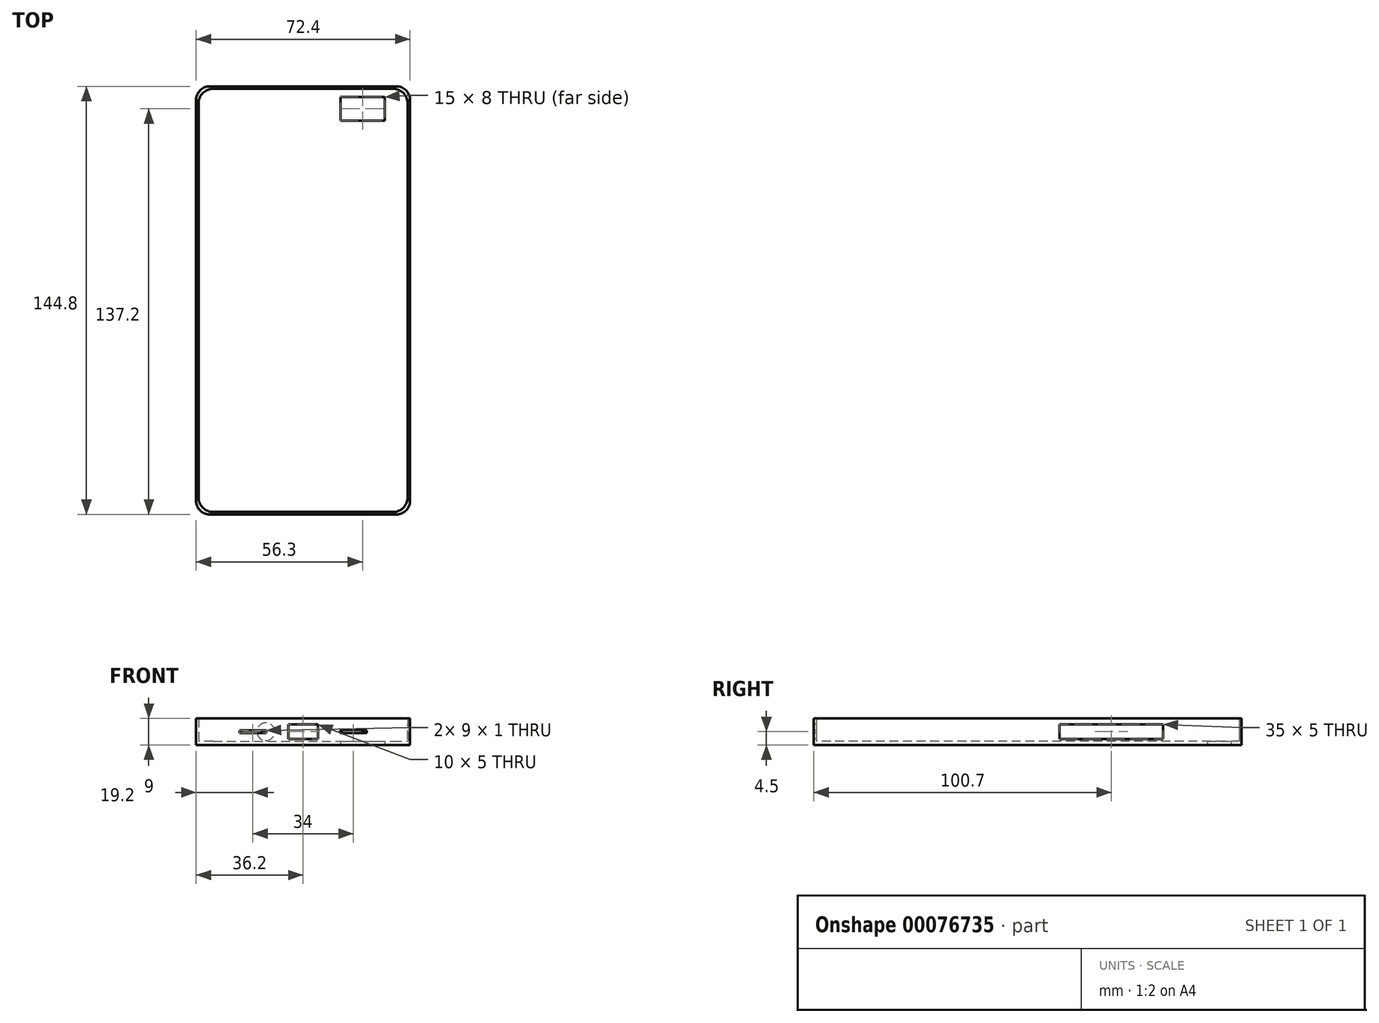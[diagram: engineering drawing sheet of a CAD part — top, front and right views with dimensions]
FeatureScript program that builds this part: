
annotation { "Feature Type Name" : "Feature", "Feature Type Description" : "" }
export const myFeature = defineFeature(function(context is Context, id is Id, definition is map)
    precondition{}
    {
        {
            var Q0;
            Q0=qCreatedBy(makeId("Top.planeOp"),FACE);
            var sketch = newSketch(context, id + "F0", { "sketchPlane" : qUnion([Q0])});
            skLineSegment(sketch, "E0.bottom", {"start": v(30.4, -71.6) * mm, "end": v(-30.4, -71.6) * mm});
            skLineSegment(sketch, "E0.top", {"start": v(30.4, 71.6) * mm, "end": v(-30.4, 71.6) * mm});
            skLineSegment(sketch, "E0.left", {"start": v(35.4, -66.6) * mm, "end": v(35.4, 66.6) * mm});
            skLineSegment(sketch, "E0.right", {"start": v(-35.4, -66.6) * mm, "end": v(-35.4, 66.6) * mm});
            skPoint(sketch, "E0.middle", {"position": v(0, 0) * mm});
            skLineSegment(sketch, "E1.bottom", {"start": v(31.6, -72.8) * mm, "end": v(-31.6, -72.8) * mm});
            skLineSegment(sketch, "E1.top", {"start": v(31.6, 72.8) * mm, "end": v(-31.6, 72.8) * mm});
            skLineSegment(sketch, "E1.left", {"start": v(36.6, -67.8) * mm, "end": v(36.6, 67.8) * mm});
            skLineSegment(sketch, "E1.right", {"start": v(-36.6, -67.8) * mm, "end": v(-36.6, 67.8) * mm});
            skPoint(sketch, "E2.visualSharp", {"position": v(35.4, 71.6) * mm});
            skArc(sketch, "E2.filletArc", {"start": v(35.4, 66.6) * mm, "mid": v(33.94, 70.14) * mm, "end": v(30.4, 71.6) * mm});
            skPoint(sketch, "E3.visualSharp", {"position": v(-35.4, 71.6) * mm});
            skArc(sketch, "E3.filletArc", {"start": v(-30.4, 71.6) * mm, "mid": v(-33.94, 70.14) * mm, "end": v(-35.4, 66.6) * mm});
            skPoint(sketch, "E4.visualSharp", {"position": v(-35.4, -71.6) * mm});
            skArc(sketch, "E4.filletArc", {"start": v(-35.4, -66.6) * mm, "mid": v(-33.94, -70.14) * mm, "end": v(-30.4, -71.6) * mm});
            skPoint(sketch, "E5.visualSharp", {"position": v(35.4, -71.6) * mm});
            skArc(sketch, "E5.filletArc", {"start": v(30.4, -71.6) * mm, "mid": v(33.94, -70.14) * mm, "end": v(35.4, -66.6) * mm});
            skPoint(sketch, "E6.visualSharp", {"position": v(-36.6, 72.8) * mm});
            skArc(sketch, "E6.filletArc", {"start": v(-31.6, 72.8) * mm, "mid": v(-35.14, 71.34) * mm, "end": v(-36.6, 67.8) * mm});
            skPoint(sketch, "E7.visualSharp", {"position": v(36.6, 72.8) * mm});
            skArc(sketch, "E7.filletArc", {"start": v(36.6, 67.8) * mm, "mid": v(35.14, 71.34) * mm, "end": v(31.6, 72.8) * mm});
            skPoint(sketch, "E8.visualSharp", {"position": v(36.6, -72.8) * mm});
            skArc(sketch, "E8.filletArc", {"start": v(31.6, -72.8) * mm, "mid": v(35.14, -71.34) * mm, "end": v(36.6, -67.8) * mm});
            skPoint(sketch, "E9.visualSharp", {"position": v(-36.6, -72.8) * mm});
            skArc(sketch, "E9.filletArc", {"start": v(-36.6, -67.8) * mm, "mid": v(-35.14, -71.34) * mm, "end": v(-31.6, -72.8) * mm});
            skSolve(sketch);
        }
        {
            var Q0;
            Q0=makeQuery(id+"F0.imprint","IMPRINT",FACE,{"disambiguationData":[TD([[makeQuery(id+"F0.imprint","IMPRINT",EDGE,{"derivedFrom":sQuery(id+"F0.wireOp",EDGE,"E0.bottom")}),-1.0]])]});
            var Q1;
            Q1=makeQuery(id+"F0.imprint","IMPRINT",FACE,{"disambiguationData":[TD([[makeQuery(id+"F0.imprint","IMPRINT",EDGE,{"derivedFrom":sQuery(id+"F0.wireOp",EDGE,"E0.bottom")}),1.0]])]});
            extrude(context, id + "F1", {"entities" : qUnion([Q0, Q1]), "depth" : 1.2 * mm});
        }
        {
            var Q0;
            Q0=makeQuery(id+"F0.imprint","IMPRINT",FACE,{"disambiguationData":[TD([[makeQuery(id+"F0.imprint","IMPRINT",EDGE,{"derivedFrom":sQuery(id+"F0.wireOp",EDGE,"E0.bottom")}),1.0]])]});
            extrude(context, id + "F2", {"entities" : qUnion([Q0]), "operationType" : NewBodyOperationType.ADD, "depth" : 9 * mm});
        }
        {
            var Q0;
            {var subQ0=sQuery(id+"F0.wireOp",EDGE,"E1.left");Q0=makeQuery(id+"F2.boolean.opBoolean","MERGE",FACE,{"derivedFrom":[makeQuery(id+"F1.opExtrude","SWEPT_FACE",FACE,{"disambiguationData":[OSD([subQ0])]}),makeQuery(id+"F2.opExtrude","SWEPT_FACE",FACE,{"disambiguationData":[OSD([subQ0])]})]});}
            var sketch = newSketch(context, id + "F3", { "sketchPlane" : qUnion([Q0])});
            skLineSegment(sketch, "E10.bottom", {"start": v(26.1, 2) * mm, "end": v(45.8, 2) * mm});
            skLineSegment(sketch, "E10.top", {"start": v(26.1, 7) * mm, "end": v(45.8, 7) * mm});
            skLineSegment(sketch, "E10.right", {"start": v(45.8, 2) * mm, "end": v(45.8, 7) * mm});
            skPoint(sketch, "E10.middle", {"position": v(35.95, 4.5) * mm});
            skPoint(sketch, "E10.middle.positionSnap0", {"position": v(67.8, 4.5) * mm});
            skPoint(sketch, "E10.centerSnap0", {"position": v(67.8, 4.5) * mm});
            skLineSegment(sketch, "E11.bottom", {"start": v(19.8, 2) * mm, "end": v(10.8, 2) * mm});
            skLineSegment(sketch, "E11.top", {"start": v(19.8, 7) * mm, "end": v(10.8, 7) * mm});
            skLineSegment(sketch, "E11.right", {"start": v(10.8, 2) * mm, "end": v(10.8, 7) * mm});
            skPoint(sketch, "E11.middle", {"position": v(15.3, 4.5) * mm});
            skPoint(sketch, "E11.cornerSnap0", {"position": v(35.95, 2) * mm});
            skLineSegment(sketch, "E12", {"start": v(19.8, 2) * mm, "end": v(26.1, 2) * mm});
            skLineSegment(sketch, "E13", {"start": v(26.1, 7) * mm, "end": v(19.8, 7) * mm});
            skSolve(sketch);
        }
        {
            var Q0;
            Q0 = qSketchRegion(id + "F3", true);
            extrude(context, id + "F4", {"entities" : qUnion([Q0]), "operationType" : NewBodyOperationType.REMOVE, "endBound" : BoundingType.UP_TO_NEXT, "oppositeDirection" : true, "depth" : 25 * mm});
        }
        {
            var Q0;
            {var subQ0=sQuery(id+"F0.wireOp",EDGE,"E1.bottom");Q0=makeQuery(id+"F2.boolean.opBoolean","MERGE",FACE,{"derivedFrom":[makeQuery(id+"F1.opExtrude","SWEPT_FACE",FACE,{"disambiguationData":[OSD([subQ0])]}),makeQuery(id+"F2.opExtrude","SWEPT_FACE",FACE,{"disambiguationData":[OSD([subQ0])]})]});}
            var sketch = newSketch(context, id + "F5", { "sketchPlane" : qUnion([Q0])});
            skPoint(sketch, "E14.middle.positionSnap0", {"position": v(31.6, 4.5) * mm});
            skPoint(sketch, "E14.centerSnap0", {"position": v(31.6, 4.5) * mm});
            skLineSegment(sketch, "E15.bottom", {"start": v(5, 2) * mm, "end": v(-5, 2) * mm});
            skLineSegment(sketch, "E15.top", {"start": v(5, 7) * mm, "end": v(-5, 7) * mm});
            skLineSegment(sketch, "E15.left", {"start": v(5, 2) * mm, "end": v(5, 7) * mm});
            skLineSegment(sketch, "E15.right", {"start": v(-5, 2) * mm, "end": v(-5, 7) * mm});
            skPoint(sketch, "E15.middle", {"position": v(0, 4.5) * mm});
            skSolve(sketch);
        }
        {
            var Q0;
            Q0 = qSketchRegion(id + "F5", true);
            extrude(context, id + "F6", {"entities" : qUnion([Q0]), "operationType" : NewBodyOperationType.REMOVE, "endBound" : BoundingType.UP_TO_NEXT, "oppositeDirection" : true, "depth" : 25 * mm});
        }
        {
            var Q0;
            {var subQ0=sQuery(id+"F0.wireOp",EDGE,"E1.bottom");Q0=makeQuery(id+"F2.boolean.opBoolean","MERGE",FACE,{"derivedFrom":[makeQuery(id+"F1.opExtrude","SWEPT_FACE",FACE,{"disambiguationData":[OSD([subQ0])]}),makeQuery(id+"F2.opExtrude","SWEPT_FACE",FACE,{"disambiguationData":[OSD([subQ0])]})]});}
            var sketch = newSketch(context, id + "F7", { "sketchPlane" : qUnion([Q0])});
            skPoint(sketch, "E16.middle.positionSnap0", {"position": v(-5, 4.5) * mm});
            skPoint(sketch, "E16.cornerSnap0", {"position": v(0, 3.5) * mm});
            skPoint(sketch, "E16.centerSnap0", {"position": v(-5, 4.5) * mm});
            skLineSegment(sketch, "E17.bottom", {"start": v(-12.5, 4) * mm, "end": v(-21.5, 4) * mm});
            skLineSegment(sketch, "E17.top", {"start": v(-12.5, 5) * mm, "end": v(-21.5, 5) * mm});
            skLineSegment(sketch, "E17.left", {"start": v(-12.5, 4) * mm, "end": v(-12.5, 5) * mm});
            skLineSegment(sketch, "E17.right", {"start": v(-21.5, 4) * mm, "end": v(-21.5, 5) * mm});
            skPoint(sketch, "E17.middle", {"position": v(-17, 4.5) * mm});
            skPoint(sketch, "E17.middle.positionSnap0", {"position": v(5, 4.5) * mm});
            skPoint(sketch, "E17.centerSnap0", {"position": v(5, 4.5) * mm});
            skLineSegment(sketch, "E18.MirrorCS", {"start": v(12.5, 4) * mm, "end": v(21.5, 4) * mm});
            skLineSegment(sketch, "E19.MirrorCS", {"start": v(12.5, 5) * mm, "end": v(21.5, 5) * mm});
            skLineSegment(sketch, "E20.MirrorCS", {"start": v(12.5, 4) * mm, "end": v(12.5, 5) * mm});
            skLineSegment(sketch, "E21.MirrorCS", {"start": v(21.5, 4) * mm, "end": v(21.5, 5) * mm});
            skPoint(sketch, "E22.MirrorP", {"position": v(17, 4.5) * mm});
            skSolve(sketch);
        }
        {
            var Q0;
            Q0=makeQuery(id+"F7.imprint","IMPRINT",FACE,{"disambiguationData":[TD([[makeQuery(id+"F7.imprint","IMPRINT",EDGE,{"derivedFrom":sQuery(id+"F7.wireOp",EDGE,"E17.bottom")}),-1.0]])]});
            var Q1;
            Q1=makeQuery(id+"F7.imprint","IMPRINT",FACE,{"disambiguationData":[TD([[makeQuery(id+"F7.imprint","IMPRINT",EDGE,{"derivedFrom":sQuery(id+"F7.wireOp",EDGE,"E18.MirrorCS")}),1.0]])]});
            extrude(context, id + "F8", {"entities" : qUnion([Q0, Q1]), "operationType" : NewBodyOperationType.REMOVE, "endBound" : BoundingType.UP_TO_NEXT, "oppositeDirection" : true, "depth" : 25 * mm});
        }
        {
            var Q0;
            Q0=makeQuery(id+"F1.opExtrude","CAP_FACE",FACE,{"disambiguationData":[OSD([sQuery(id+"F0.wireOp",EDGE,"E1.bottom"),sQuery(id+"F0.wireOp",EDGE,"E1.top"),sQuery(id+"F0.wireOp",EDGE,"E1.left"),sQuery(id+"F0.wireOp",EDGE,"E1.right"),sQuery(id+"F0.wireOp",EDGE,"E6.filletArc"),sQuery(id+"F0.wireOp",EDGE,"E7.filletArc"),sQuery(id+"F0.wireOp",EDGE,"E8.filletArc"),sQuery(id+"F0.wireOp",EDGE,"E9.filletArc")])],"isStart":true});
            var sketch = newSketch(context, id + "F9", { "sketchPlane" : qUnion([Q0])});
            skLineSegment(sketch, "E23.bottom", {"start": v(12.6, -60.8) * mm, "end": v(27.6, -60.8) * mm});
            skLineSegment(sketch, "E23.top", {"start": v(12.6, -68.8) * mm, "end": v(27.6, -68.8) * mm});
            skLineSegment(sketch, "E23.left", {"start": v(12.6, -60.8) * mm, "end": v(12.6, -68.8) * mm});
            skLineSegment(sketch, "E23.right", {"start": v(27.6, -60.8) * mm, "end": v(27.6, -68.8) * mm});
            skPoint(sketch, "E23.middle", {"position": v(20.1, -64.8) * mm});
            skSolve(sketch);
        }
        {
            var Q0;
            Q0 = qSketchRegion(id + "F9", true);
            extrude(context, id + "F10", {"entities" : qUnion([Q0]), "operationType" : NewBodyOperationType.REMOVE, "endBound" : BoundingType.UP_TO_NEXT, "oppositeDirection" : true, "depth" : 25 * mm});
        }
        {
            var Q0;
            {var subQ0=sQuery(id+"F0.wireOp",EDGE,"E1.top");Q0=makeQuery(id+"F2.boolean.opBoolean","MERGE",FACE,{"derivedFrom":[makeQuery(id+"F1.opExtrude","SWEPT_FACE",FACE,{"disambiguationData":[OSD([subQ0])]}),makeQuery(id+"F2.opExtrude","SWEPT_FACE",FACE,{"disambiguationData":[OSD([subQ0])]})]});}
            var sketch = newSketch(context, id + "F11", { "sketchPlane" : qUnion([Q0])});
            skCircle(sketch, "E24", {"center": v(12.6, 4.5) * mm, "radius": 3 * mm});
            skPoint(sketch, "E24.centerSnap0", {"position": v(31.6, 4.5) * mm});
            skCircle(sketch, "E25", {"center": v(-2.6, 4.5) * mm, "radius": 1 * mm});
            skSolve(sketch);
        }
        {
            var Q0;
            Q0=makeQuery(id+"F11.imprint","IMPRINT",FACE,{"disambiguationData":[TD([[makeQuery(id+"F11.imprint","IMPRINT",EDGE,{"derivedFrom":sQuery(id+"F11.wireOp",EDGE,"E24")}),1.0]])]});
            extrude(context, id + "F12", {"entities" : qUnion([Q0]), "operationType" : NewBodyOperationType.REMOVE, "endBound" : BoundingType.UP_TO_NEXT, "oppositeDirection" : true, "depth" : 25 * mm});
        }
        {
            var Q0;
            Q0=makeQuery(id+"F2.opExtrude","CAP_FACE",FACE,{"disambiguationData":[OSD([sQuery(id+"F0.wireOp",EDGE,"E0.bottom"),sQuery(id+"F0.wireOp",EDGE,"E0.top"),sQuery(id+"F0.wireOp",EDGE,"E0.left"),sQuery(id+"F0.wireOp",EDGE,"E0.right"),sQuery(id+"F0.wireOp",EDGE,"E1.bottom"),sQuery(id+"F0.wireOp",EDGE,"E1.top"),sQuery(id+"F0.wireOp",EDGE,"E1.left"),sQuery(id+"F0.wireOp",EDGE,"E1.right"),sQuery(id+"F0.wireOp",EDGE,"E2.filletArc"),sQuery(id+"F0.wireOp",EDGE,"E3.filletArc"),sQuery(id+"F0.wireOp",EDGE,"E4.filletArc"),sQuery(id+"F0.wireOp",EDGE,"E5.filletArc"),sQuery(id+"F0.wireOp",EDGE,"E6.filletArc"),sQuery(id+"F0.wireOp",EDGE,"E7.filletArc"),sQuery(id+"F0.wireOp",EDGE,"E8.filletArc"),sQuery(id+"F0.wireOp",EDGE,"E9.filletArc")])],"isStart":false});
            var sketch = newSketch(context, id + "F13", { "sketchPlane" : qUnion([Q0])});
            skLineSegment(sketch, "E26.0", {"start": v(31.6, 72.4) * mm, "end": v(-31.6, 72.4) * mm});
            skArc(sketch, "E27.0", {"start": v(36.2, 67.8) * mm, "mid": v(34.85, 71.05) * mm, "end": v(31.6, 72.4) * mm});
            skLineSegment(sketch, "E28.0", {"start": v(36.2, -67.8) * mm, "end": v(36.2, 67.8) * mm});
            skArc(sketch, "E29.0", {"start": v(-31.6, 72.4) * mm, "mid": v(-34.85, 71.05) * mm, "end": v(-36.2, 67.8) * mm});
            skArc(sketch, "E30.0", {"start": v(-36.2, -67.8) * mm, "mid": v(-34.85, -71.05) * mm, "end": v(-31.6, -72.4) * mm});
            skArc(sketch, "E31.0", {"start": v(31.6, -72.4) * mm, "mid": v(34.85, -71.05) * mm, "end": v(36.2, -67.8) * mm});
            skLineSegment(sketch, "E32.0", {"start": v(31.6, -72.4) * mm, "end": v(-31.6, -72.4) * mm});
            skLineSegment(sketch, "E33.0", {"start": v(-36.2, -67.8) * mm, "end": v(-36.2, 67.8) * mm});
            skSolve(sketch);
        }
        {
            var Q0;
            Q0=makeQuery(id+"F13.imprint","IMPRINT",FACE,{"disambiguationData":[TD([[makeQuery(id+"F13.imprint","IMPRINT",EDGE,{"derivedFrom":sQuery(id+"F13.wireOp",EDGE,"E26.0")}),-1.0]])]});
            extrude(context, id + "F14", {"entities" : qUnion([Q0]), "operationType" : NewBodyOperationType.REMOVE, "endBound" : BoundingType.THROUGH_ALL, "oppositeDirection" : true, "depth" : 25 * mm, "offsetDistance" : 25 * mm});
        }
    });
